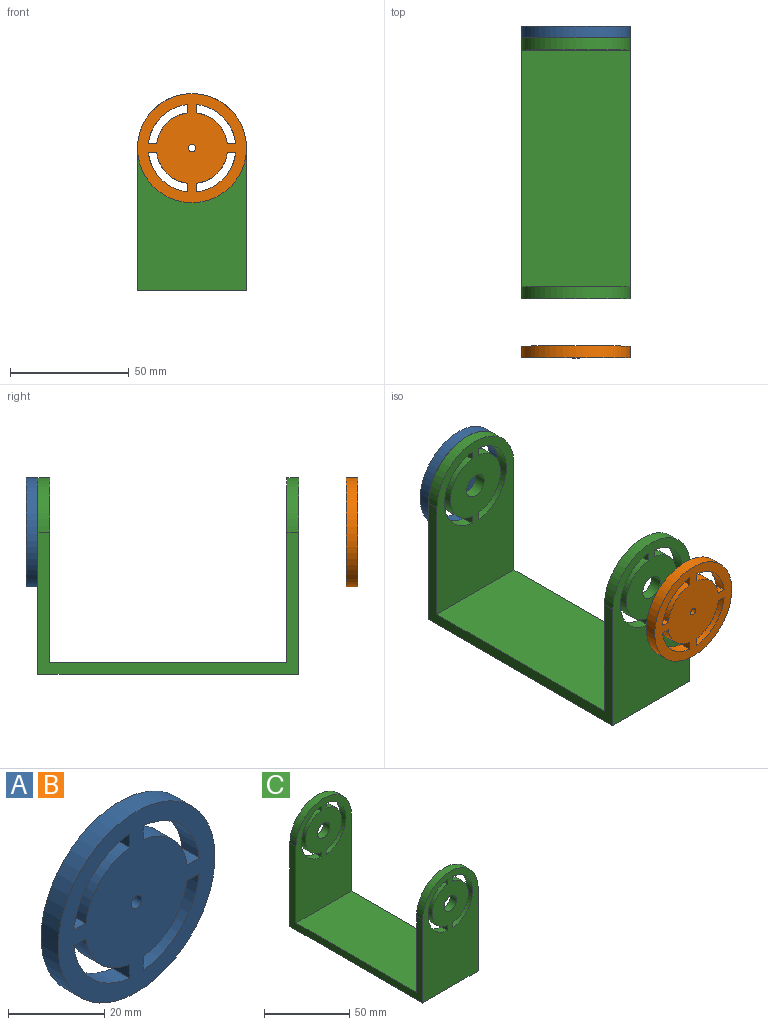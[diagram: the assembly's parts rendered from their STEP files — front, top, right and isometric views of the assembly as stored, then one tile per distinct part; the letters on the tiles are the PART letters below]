
ASSEMBLY  parts=3 mates=1
PART A: 20 faces, bbox 46x5x46 mm
  f0: cylinder r=15mm len=12.87mm, axis (0,1,0), area 97.7mm2, adj f5,f6,f8,f18
  f1: cylinder r=15mm len=12.87mm, axis (0,1,0), area 97.7mm2, adj f5,f6,f9,f11
  f2: cylinder r=15mm len=12.87mm, axis (0,1,0), area 97.7mm2, adj f5,f6,f12,f14
  f3: cylinder r=15mm len=12.87mm, axis (0,1,0), area 97.7mm2, adj f5,f6,f15,f17
  f4: cylinder r=1.55mm len=5mm, axis (0,1,0), area 48.7mm2, adj f5,f6
  f5: plane 46x46mm, normal (0,-1,0), area 1342.1mm2, adj f0,f1,f2,f3,f4,f7,f8,f9
  f6: plane 46x46mm, normal (0,1,0), area 1342.1mm2, adj f0,f1,f2,f3,f4,f7,f8,f9
  f7: cylinder r=18.5mm len=16.39mm, axis (0,-1,0), area 125.3mm2, adj f5,f6,f8,f18
  f8: plane 5x3.53mm, normal (1,0,0), area 17.6mm2, adj f0,f5,f6,f7
  f9: plane 5x3.53mm, normal (-1,0,0), area 17.6mm2, adj f1,f5,f6,f10
  f10: cylinder r=18.5mm len=16.39mm, axis (0,-1,0), area 125.3mm2, adj f5,f6,f9,f11
  f11: plane 5x3.53mm, normal (0,0,-1), area 17.6mm2, adj f1,f5,f6,f10
  f12: plane 5x3.53mm, normal (0,0,1), area 17.6mm2, adj f2,f5,f6,f13
  f13: cylinder r=18.5mm len=16.39mm, axis (0,-1,0), area 125.3mm2, adj f5,f6,f12,f14
  f14: plane 5x3.53mm, normal (-1,0,0), area 17.6mm2, adj f2,f5,f6,f13
  f15: plane 5x3.53mm, normal (1,0,0), area 17.6mm2, adj f3,f5,f6,f16
  f16: cylinder r=18.5mm len=16.39mm, axis (0,-1,0), area 125.3mm2, adj f5,f6,f15,f17
  f17: plane 5x3.53mm, normal (0,0,1), area 17.6mm2, adj f3,f5,f6,f16
  f18: plane 5x3.53mm, normal (0,0,-1), area 17.6mm2, adj f0,f5,f6,f7
  f19: cylinder r=23mm len=46mm, axis (0,-1,0), area 722.6mm2, adj f5,f6
PART B: same geometry as A
PART C: 28 faces, bbox 46x110x83 mm
  f0: plane 83x46mm, normal (0,-1,0), area 3165.7mm2, adj f5,f6,f7,f8,f11,f20,f21,f22
  f1: plane 78x46mm, normal (0,1,0), area 2935.7mm2, adj f4,f5,f6,f7,f11,f20,f21,f22
  f2: plane 83x46mm, normal (0,1,0), area 3165.7mm2, adj f5,f7,f8,f9,f10,f12,f13,f14
  f3: plane 78x46mm, normal (0,-1,0), area 2935.7mm2, adj f4,f5,f7,f9,f10,f12,f13,f14
  f4: plane 100x46mm, normal (0,0,1), area 4600mm2, adj f1,f3,f5,f7
  f5: plane 110x60mm, normal (1,0,0), area 1100mm2, adj f0,f1,f2,f3,f4,f6,f8,f9
  f6: cylinder r=23mm len=46mm, axis (0,1,0), area 361.3mm2, adj f0,f1,f5,f7
  f7: plane 110x60mm, normal (-1,0,0), area 1100mm2, adj f0,f1,f2,f3,f4,f6,f8,f9
  f8: plane 110x46mm, normal (0,0,-1), area 5060mm2, adj f0,f2,f5,f7
  f9: cylinder r=23mm len=46mm, axis (0,1,0), area 361.3mm2, adj f2,f3,f5,f7
  f10: cylinder r=5.2mm len=10.4mm, axis (0,-1,0), area 163.4mm2, adj f2,f3
  f11: cylinder r=5.2mm len=10.4mm, axis (0,-1,0), area 163.4mm2, adj f0,f1
  f12: plane 5x3.53mm, normal (1,0,0), area 17.6mm2, adj f2,f3,f13,f15
  f13: cylinder r=15mm len=29.73mm, axis (0,-1,0), area 215.6mm2, adj f2,f3,f12,f14
  f14: plane 5x3.53mm, normal (1,0,0), area 17.6mm2, adj f2,f3,f13,f15
  f15: cylinder r=18.5mm len=36.78mm, axis (0,-1,0), area 270.6mm2, adj f2,f3,f12,f14
  f16: cylinder r=15mm len=29.73mm, axis (0,-1,0), area 215.6mm2, adj f2,f3,f17,f19
  f17: plane 5x3.53mm, normal (-1,0,0), area 17.6mm2, adj f2,f3,f16,f18
  f18: cylinder r=18.5mm len=36.78mm, axis (0,-1,0), area 270.6mm2, adj f2,f3,f17,f19
  f19: plane 5x3.53mm, normal (-1,0,0), area 17.6mm2, adj f2,f3,f16,f18
  f20: cylinder r=18.5mm len=36.78mm, axis (0,-1,0), area 270.6mm2, adj f0,f1,f21,f23
  f21: plane 5x3.53mm, normal (1,0,0), area 17.6mm2, adj f0,f1,f20,f22
  f22: cylinder r=15mm len=29.73mm, axis (0,-1,0), area 215.6mm2, adj f0,f1,f21,f23
  f23: plane 5x3.53mm, normal (1,0,0), area 17.6mm2, adj f0,f1,f20,f22
  f24: plane 5x3.53mm, normal (-1,0,0), area 17.6mm2, adj f0,f1,f25,f27
  f25: cylinder r=18.5mm len=36.78mm, axis (0,-1,0), area 270.6mm2, adj f0,f1,f24,f26
  f26: plane 5x3.53mm, normal (-1,0,0), area 17.6mm2, adj f0,f1,f25,f27
  f27: cylinder r=15mm len=29.73mm, axis (0,-1,0), area 215.6mm2, adj f0,f1,f24,f26
PLACE A rot(axis=(1,0,0),180deg) t=(5.46,66.25,-24.52)mm
PLACE B rot(axis=(1,0,0),180deg) t=(5.46,-68.75,-24.52)mm
PLACE C t=(5.46,-38.75,-24.52)mm fixed
MATE revolute A.f19 <-> C.f16  axis (0,-1,0) through (5.46,66.25,-24.52)mm
